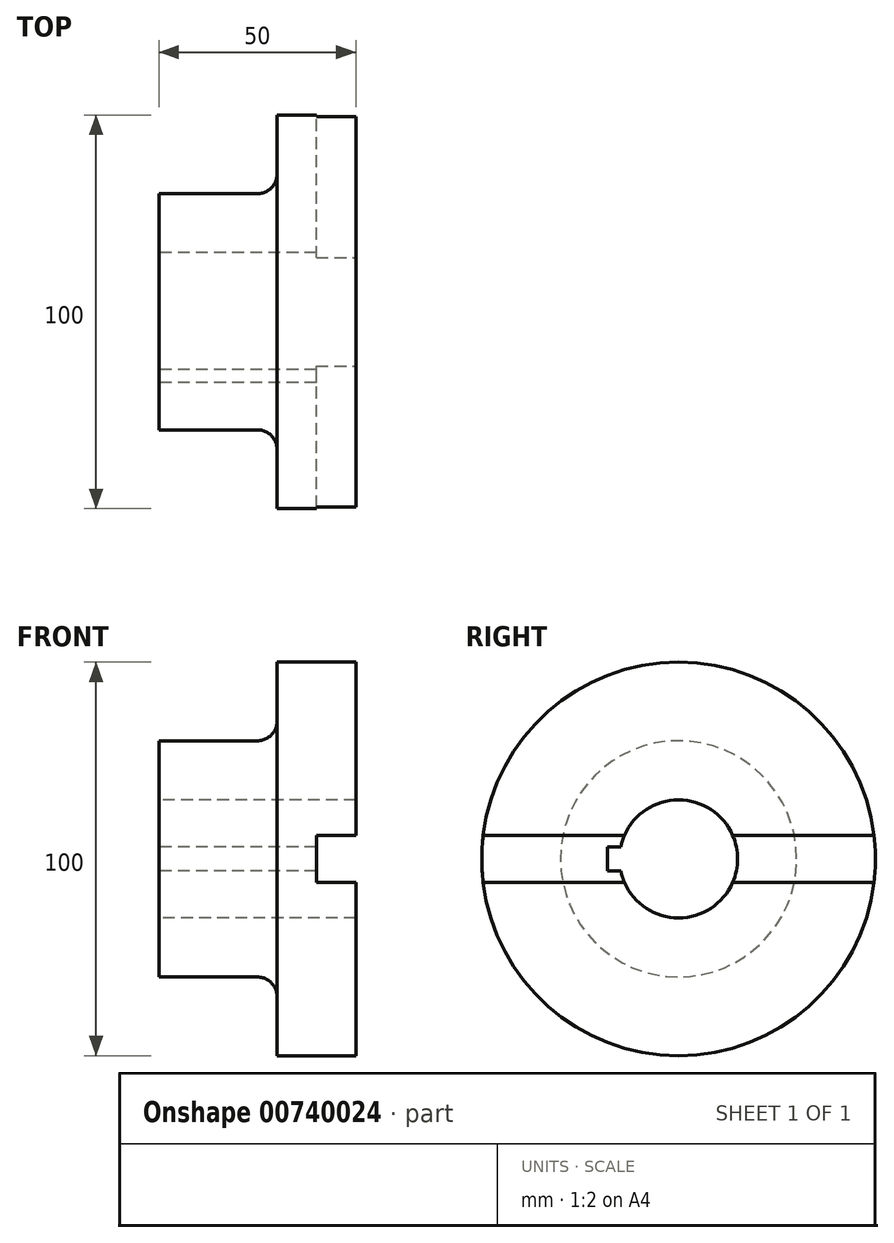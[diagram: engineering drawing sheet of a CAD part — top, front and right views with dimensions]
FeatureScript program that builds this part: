
annotation { "Feature Type Name" : "Feature", "Feature Type Description" : "" }
export const myFeature = defineFeature(function(context is Context, id is Id, definition is map)
    precondition{}
    {
        {
            var Q0;
            Q0=qCreatedBy(makeId("Front.planeOp"),FACE);
            var sketch = newSketch(context, id + "F0", { "sketchPlane" : qUnion([Q0])});
            skLineSegment(sketch, "E0", {"start": v(0, 15) * mm, "end": v(0, 30) * mm});
            skLineSegment(sketch, "E1", {"start": v(0, 30) * mm, "end": v(25, 30) * mm});
            skLineSegment(sketch, "E2", {"start": v(30, 35) * mm, "end": v(30, 50) * mm});
            skLineSegment(sketch, "E3", {"start": v(30, 50) * mm, "end": v(50, 50) * mm});
            skLineSegment(sketch, "E4", {"start": v(50, 50) * mm, "end": v(50, 15) * mm});
            skLineSegment(sketch, "E5", {"start": v(50, 15) * mm, "end": v(0, 15) * mm});
            skArc(sketch, "E6.filletArc", {"start": v(25, 30) * mm, "mid": v(28.54, 31.46) * mm, "end": v(30, 35) * mm});
            skLineSegment(sketch, "E7", {"start": v(0, 0) * mm, "end": v(36.28, 0) * mm});
            skSolve(sketch);
        }
        {
            var Q0;
            Q0=makeQuery(id+"F0.imprint","IMPRINT",FACE,{"disambiguationData":[TD([[makeQuery(id+"F0.imprint","IMPRINT",EDGE,{"derivedFrom":sQuery(id+"F0.wireOp",EDGE,"E0")}),-1.0]])]});
            var Q1;
            Q1=sQuery(id+"F0.wireOp",EDGE,"E7");
            revolve(context, id + "F1", {"surfaceOperationType" : NewSurfaceOperationType.NEW, "entities" : qUnion([Q0]), "axis" : qUnion([Q1]), "revolveType" : RevolveType.FULL});
        }
        {
            var Q0;
            Q0=makeQuery(id+"F1.opRevolve","SWEPT_FACE",FACE,{"disambiguationData":[OSD([sQuery(id+"F0.wireOp",EDGE,"E0")])]});
            var sketch = newSketch(context, id + "F2", { "sketchPlane" : qUnion([Q0])});
            skArc(sketch, "E8", {"start": v(14.7, -3) * mm, "mid": v(15, 0) * mm, "end": v(14.7, 3) * mm});
            skLineSegment(sketch, "E9", {"start": v(18, -3) * mm, "end": v(14.7, -3) * mm});
            skLineSegment(sketch, "E10", {"start": v(18, 3) * mm, "end": v(14.7, 3) * mm});
            skLineSegment(sketch, "E11", {"start": v(18, 3) * mm, "end": v(18, -3) * mm});
            skSolve(sketch);
        }
        {
            var Q0;
            Q0=makeQuery(id+"F2.imprint","IMPRINT",FACE,{"disambiguationData":[TD([[makeQuery(id+"F2.imprint","IMPRINT",EDGE,{"derivedFrom":sQuery(id+"F2.wireOp",EDGE,"E8")}),-1.0]])]});
            extrude(context, id + "F3", {"entities" : qUnion([Q0]), "operationType" : NewBodyOperationType.REMOVE, "oppositeDirection" : true, "depth" : 50 * mm, "offsetDistance" : 25 * mm});
        }
        {
            var Q0;
            Q0=makeQuery(id+"F1.opRevolve","SWEPT_FACE",FACE,{"disambiguationData":[OSD([sQuery(id+"F0.wireOp",EDGE,"E4")])]});
            var sketch = newSketch(context, id + "F4", { "sketchPlane" : qUnion([Q0])});
            skLineSegment(sketch, "E12.bottom", {"start": v(-49.64, 6) * mm, "end": v(49.64, 6) * mm});
            skLineSegment(sketch, "E12.top", {"start": v(-49.64, -6) * mm, "end": v(49.64, -6) * mm});
            skPoint(sketch, "E12.middle", {"position": v(0, 0) * mm});
            skArc(sketch, "E13", {"start": v(-49.64, 6) * mm, "mid": v(-50, 0) * mm, "end": v(-49.64, -6) * mm});
            skArc(sketch, "E14.trimOffspring", {"start": v(49.64, -6) * mm, "mid": v(50, 0) * mm, "end": v(49.64, 6) * mm});
            skSolve(sketch);
        }
        {
            var Q0;
            {var subQ0=sQuery(id+"F4.wireOp",EDGE,"E13");Q0=makeQuery(id+"F4.imprint","IMPRINT",FACE,{"disambiguationData":[TD([[makeQuery(id+"F4.imprint","IMPRINT",EDGE,{"derivedFrom":subQ0}),-1.0]])]});}
            var Q1;
            {var subQ0=sQuery(id+"F4.wireOp",EDGE,"E14.trimOffspring");Q1=makeQuery(id+"F4.imprint","IMPRINT",FACE,{"disambiguationData":[TD([[makeQuery(id+"F4.imprint","IMPRINT",EDGE,{"derivedFrom":subQ0}),-1.0]])]});}
            extrude(context, id + "F5", {"entities" : qUnion([Q0, Q1]), "operationType" : NewBodyOperationType.REMOVE, "oppositeDirection" : true, "depth" : 10 * mm, "offsetDistance" : 25 * mm});
        }
    });
